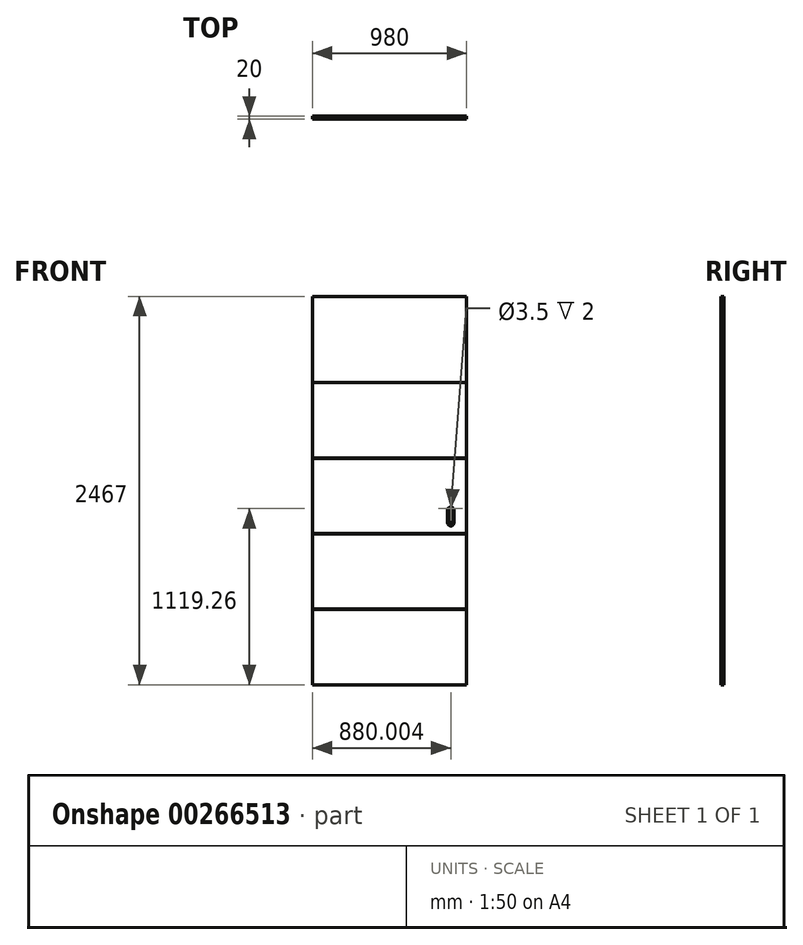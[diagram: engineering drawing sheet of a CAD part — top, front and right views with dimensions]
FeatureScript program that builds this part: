
annotation { "Feature Type Name" : "Feature", "Feature Type Description" : "" }
export const myFeature = defineFeature(function(context is Context, id is Id, definition is map)
    precondition{}
    {
        {
            var Q0;
            Q0=qCreatedBy(makeId("Front.planeOp"),FACE);
            var sketch = newSketch(context, id + "F0", { "sketchPlane" : qUnion([Q0])});
            skLineSegment(sketch, "E0.bottom", {"start": v(-661.76, 1229.1) * mm, "end": v(318.24, 1229.1) * mm});
            skLineSegment(sketch, "E0.top", {"start": v(-661.76, -1237.9) * mm, "end": v(318.24, -1237.9) * mm});
            skLineSegment(sketch, "E0.left", {"start": v(-661.76, 1229.1) * mm, "end": v(-661.76, -1237.9) * mm});
            skLineSegment(sketch, "E0.right", {"start": v(318.24, 1229.1) * mm, "end": v(318.24, -1237.9) * mm});
            skSolve(sketch);
        }
        {
            var Q0;
            Q0=makeQuery(id+"F0.imprint","IMPRINT",FACE,{"disambiguationData":[TD([[makeQuery(id+"F0.imprint","IMPRINT",EDGE,{"derivedFrom":sQuery(id+"F0.wireOp",EDGE,"E0.bottom")}),-1.0]])]});
            extrude(context, id + "F1", {"entities" : qUnion([Q0]), "depth" : 18 * mm});
        }
        {
            var Q0;
            Q0=makeQuery(id+"F1.opExtrude","SWEPT_FACE",FACE,{"disambiguationData":[OSD([sQuery(id+"F0.wireOp",EDGE,"E0.left")])]});
            var sketch = newSketch(context, id + "F2", { "sketchPlane" : qUnion([Q0])});
            skLineSegment(sketch, "E1", {"start": v(-467.06, -757.9) * mm, "end": v(625.08, -757.9) * mm, "construction": true});
            skLineSegment(sketch, "E2", {"start": v(625.08, -277.9) * mm, "end": v(-589.97, -277.9) * mm, "construction": true});
            skLineSegment(sketch, "E3", {"start": v(-589.97, 202.1) * mm, "end": v(575.92, 202.1) * mm, "construction": true});
            skLineSegment(sketch, "E4", {"start": v(575.92, 682.1) * mm, "end": v(-586.45, 682.1) * mm, "construction": true});
            skLineSegment(sketch, "E5", {"start": v(-586.45, 1229.1) * mm, "end": v(554.85, 1229.1) * mm, "construction": true});
            skLineSegment(sketch, "E6", {"start": v(0, -1237.9) * mm, "end": v(-639.13, -1237.9) * mm, "construction": true});
            skLineSegment(sketch, "E7", {"start": v(18, -756.9) * mm, "end": v(17, -757.9) * mm});
            skLineSegment(sketch, "E8", {"start": v(18, -756.9) * mm, "end": v(18, -757.9) * mm});
            skLineSegment(sketch, "E9.MirrorCS", {"start": v(18, -758.9) * mm, "end": v(17, -757.9) * mm});
            skLineSegment(sketch, "E10.MirrorCS", {"start": v(18, -758.9) * mm, "end": v(18, -757.9) * mm});
            skLineSegment(sketch, "E11", {"start": v(384.77, -277.9) * mm, "end": v(384.77, -757.9) * mm, "construction": true});
            skLineSegment(sketch, "E12", {"start": v(384.77, -517.9) * mm, "end": v(-286.08, -517.9) * mm, "construction": true});
            skLineSegment(sketch, "E13.MirrorCS", {"start": v(18, 683.1) * mm, "end": v(18, 682.1) * mm});
            skLineSegment(sketch, "E14.MirrorCS", {"start": v(18, 683.1) * mm, "end": v(17, 682.1) * mm});
            skLineSegment(sketch, "E15.MirrorCS", {"start": v(18, 681.1) * mm, "end": v(17, 682.1) * mm});
            skLineSegment(sketch, "E16.MirrorCS", {"start": v(18, 681.1) * mm, "end": v(18, 682.1) * mm});
            skLineSegment(sketch, "E17.MirrorCS", {"start": v(18, -278.9) * mm, "end": v(18, -277.9) * mm});
            skLineSegment(sketch, "E18.MirrorCS", {"start": v(18, -276.9) * mm, "end": v(17, -277.9) * mm});
            skLineSegment(sketch, "E19.MirrorCS", {"start": v(18, -278.9) * mm, "end": v(17, -277.9) * mm});
            skLineSegment(sketch, "E20.MirrorCS", {"start": v(18, -276.9) * mm, "end": v(18, -277.9) * mm});
            skLineSegment(sketch, "E21.MirrorCS", {"start": v(18, 201.1) * mm, "end": v(18, 202.1) * mm});
            skLineSegment(sketch, "E22.MirrorCS", {"start": v(18, 203.1) * mm, "end": v(17, 202.1) * mm});
            skLineSegment(sketch, "E23.MirrorCS", {"start": v(18, 201.1) * mm, "end": v(17, 202.1) * mm});
            skLineSegment(sketch, "E24.MirrorCS", {"start": v(18, 203.1) * mm, "end": v(18, 202.1) * mm});
            skSolve(sketch);
        }
        {
            var Q0;
            Q0=qSketchRegion(id+"F2",true);
            extrude(context, id + "F3", {"entities" : qUnion([Q0]), "operationType" : NewBodyOperationType.REMOVE, "endBound" : BoundingType.THROUGH_ALL, "oppositeDirection" : true, "depth" : 25 * mm});
        }
        {
            var Q0;
            {var subQ0=sQuery(id+"F0.wireOp",EDGE,"E0.left");var subQ1=sQuery(id+"F0.wireOp",EDGE,"E0.right");Q0=makeQuery(id+"F3.boolean.opBoolean","SPLIT",FACE,{"disambiguationData":[TD([makeQuery(id+"F3.opExtrude","SWEPT_FACE",FACE,{"disambiguationData":[OSD([sQuery(id+"F2.wireOp",EDGE,"E18.MirrorCS")])]})])],"derivedFrom":makeQuery(id+"F1.opExtrude","CAP_FACE",FACE,{"disambiguationData":[OSD([sQuery(id+"F0.wireOp",EDGE,"E0.bottom"),sQuery(id+"F0.wireOp",EDGE,"E0.top"),subQ0,subQ1])],"isStart":false})});}
            var sketch = newSketch(context, id + "F4", { "sketchPlane" : qUnion([Q0])});
            skArc(sketch, "E25", {"start": v(232.24, -137.9) * mm, "mid": v(218.24, -123.9) * mm, "end": v(204.24, -137.9) * mm});
            skArc(sketch, "E26", {"start": v(204.24, -199.9) * mm, "mid": v(218.24, -213.9) * mm, "end": v(232.24, -199.9) * mm});
            skArc(sketch, "E27", {"start": v(230.24, -137.9) * mm, "mid": v(218.24, -125.9) * mm, "end": v(206.24, -137.9) * mm});
            skArc(sketch, "E28", {"start": v(206.24, -199.9) * mm, "mid": v(218.24, -211.9) * mm, "end": v(230.24, -199.9) * mm});
            skLineSegment(sketch, "E29", {"start": v(206.24, -137.9) * mm, "end": v(206.24, -199.9) * mm});
            skLineSegment(sketch, "E30", {"start": v(218.24, 69.2) * mm, "end": v(218.24, -199.9) * mm, "construction": true});
            skPoint(sketch, "E31.orphan", {"position": v(218.24, -168.9) * mm});
            skArc(sketch, "E32.trimOffspring", {"start": v(218.24, -108.9) * mm, "mid": v(204.1, -114.75) * mm, "end": v(198.24, -128.9) * mm});
            skArc(sketch, "E33.MirrorCS", {"start": v(218.24, -108.9) * mm, "mid": v(232.39, -114.75) * mm, "end": v(238.24, -128.9) * mm});
            skLineSegment(sketch, "E34.MirrorCS", {"start": v(198.24, -168.9) * mm, "end": v(198.24, -208.9) * mm});
            skArc(sketch, "E35.MirrorCS", {"start": v(218.24, -228.9) * mm, "mid": v(204.1, -223.03) * mm, "end": v(198.24, -208.9) * mm});
            skArc(sketch, "E36.MirrorCS", {"start": v(218.24, -228.9) * mm, "mid": v(232.39, -223.03) * mm, "end": v(238.24, -208.9) * mm});
            skLineSegment(sketch, "E37.MirrorCS", {"start": v(238.24, -168.9) * mm, "end": v(238.24, -208.9) * mm});
            skCircle(sketch, "E38", {"center": v(218.24, -118.63) * mm, "radius": 1.75 * mm});
            skCircle(sketch, "E39.MirrorC", {"center": v(165.33, -44.36) * mm, "radius": 1.75 * mm});
            skLineSegment(sketch, "E40", {"start": v(238.24, -128.9) * mm, "end": v(238.24, -168.9) * mm});
            skLineSegment(sketch, "E41", {"start": v(198.24, -128.9) * mm, "end": v(198.24, -168.9) * mm});
            skLineSegment(sketch, "E42", {"start": v(204.24, -199.9) * mm, "end": v(204.24, -137.9) * mm});
            skLineSegment(sketch, "E43", {"start": v(230.24, -137.9) * mm, "end": v(230.24, -199.9) * mm});
            skLineSegment(sketch, "E44", {"start": v(232.24, -137.9) * mm, "end": v(232.24, -199.9) * mm});
            skSolve(sketch);
        }
        {
            var Q0;
            Q0=makeQuery(id+"F4.imprint","IMPRINT",FACE,{"disambiguationData":[TD([[makeQuery(id+"F4.imprint","IMPRINT",EDGE,{"derivedFrom":sQuery(id+"F4.wireOp",EDGE,"E25")}),1.0]])]});
            var Q1;
            Q1=makeQuery(id+"F4.imprint","IMPRINT",FACE,{"disambiguationData":[TD([[makeQuery(id+"F4.imprint","IMPRINT",EDGE,{"derivedFrom":sQuery(id+"F4.wireOp",EDGE,"E27")}),1.0]])]});
            extrude(context, id + "F5", {"entities" : qUnion([Q0, Q1]), "operationType" : NewBodyOperationType.REMOVE, "oppositeDirection" : true, "depth" : 13 * mm});
        }
        {
            var Q0;
            Q0=makeQuery(id+"F4.imprint","IMPRINT",FACE,{"disambiguationData":[TD([[makeQuery(id+"F4.imprint","IMPRINT",EDGE,{"derivedFrom":sQuery(id+"F4.wireOp",EDGE,"E25")}),1.0]])]});
            extrude(context, id + "F6", {"entities" : qUnion([Q0]), "oppositeDirection" : true, "depth" : 13 * mm});
        }
        {
            var Q0;
            Q0=makeQuery(id+"F4.imprint","IMPRINT",FACE,{"disambiguationData":[TD([[makeQuery(id+"F4.imprint","IMPRINT",EDGE,{"derivedFrom":sQuery(id+"F4.wireOp",EDGE,"E25")}),1.0]])]});
            var Q1;
            Q1=makeQuery(id+"F4.imprint","IMPRINT",FACE,{"disambiguationData":[TD([[makeQuery(id+"F4.imprint","IMPRINT",EDGE,{"derivedFrom":sQuery(id+"F4.wireOp",EDGE,"E27")}),1.0]])]});
            extrude(context, id + "F7", {"entities" : qUnion([Q0, Q1]), "operationType" : NewBodyOperationType.ADD, "oppositeDirection" : true, "depth" : 13 * mm, "hasSecondDirection" : true, "secondDirectionOppositeDirection" : true, "secondDirectionDepth" : 11 * mm});
        }
        {
            var Q0;
            Q0=makeQuery(id+"F4.imprint","IMPRINT",FACE,{"disambiguationData":[TD([[makeQuery(id+"F4.imprint","IMPRINT",EDGE,{"derivedFrom":sQuery(id+"F4.wireOp",EDGE,"E25")}),1.0]])]});
            var Q1;
            Q1=makeQuery(id+"F4.imprint","IMPRINT",FACE,{"disambiguationData":[TD([[makeQuery(id+"F4.imprint","IMPRINT",EDGE,{"derivedFrom":sQuery(id+"F4.wireOp",EDGE,"E25")}),-1.0]])]});
            extrude(context, id + "F8", {"entities" : qUnion([Q0, Q1]), "operationType" : NewBodyOperationType.ADD, "depth" : 2 * mm});
        }
    });
